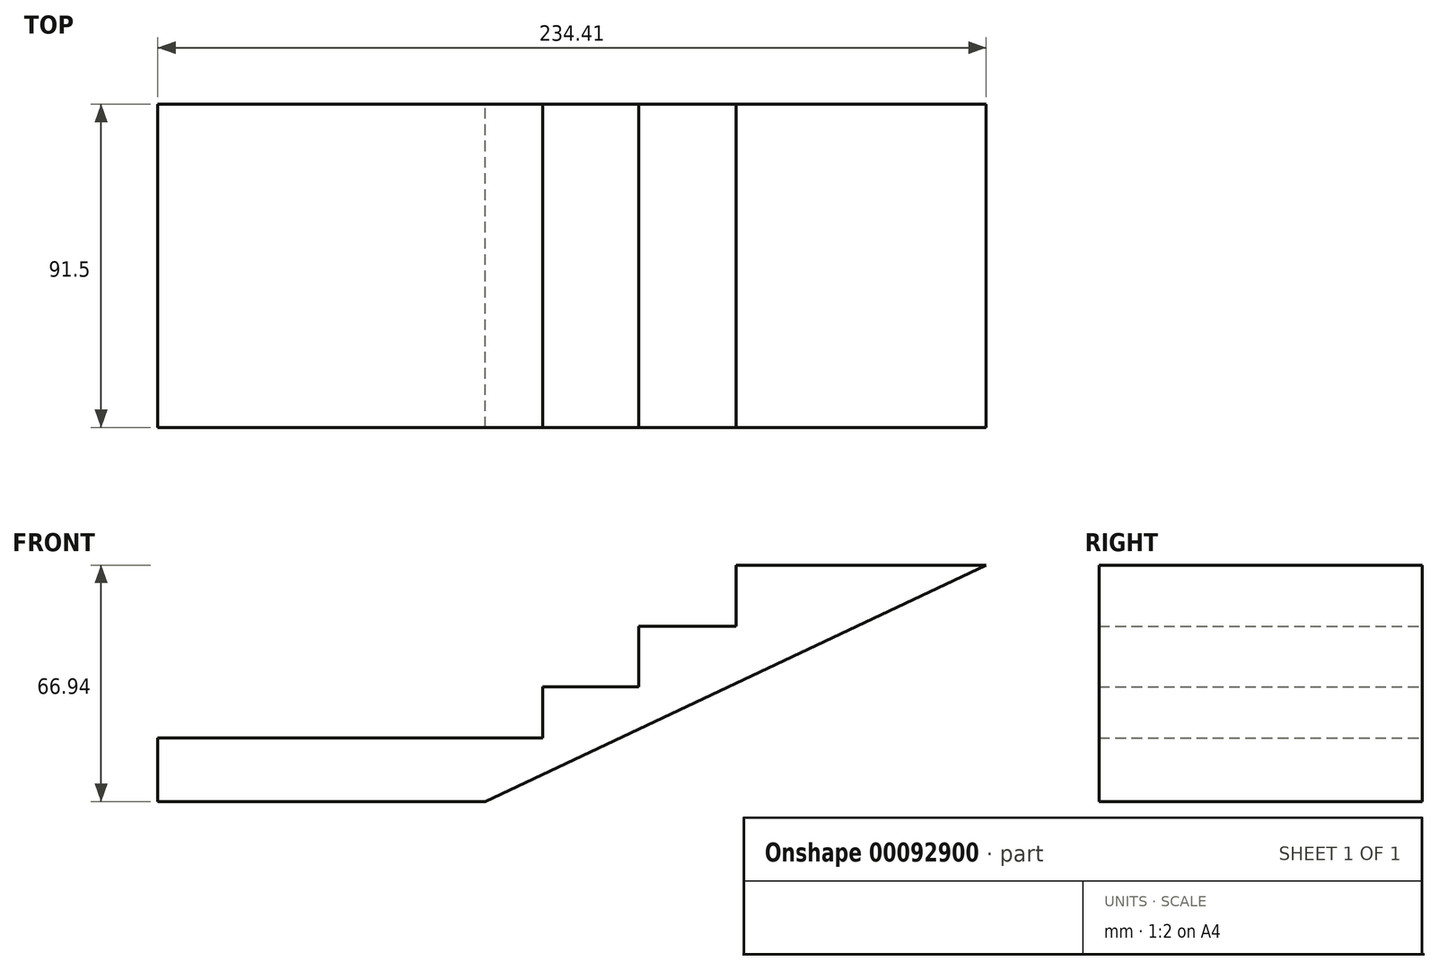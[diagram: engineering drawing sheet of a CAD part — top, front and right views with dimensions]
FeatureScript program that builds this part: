
annotation { "Feature Type Name" : "Feature", "Feature Type Description" : "" }
export const myFeature = defineFeature(function(context is Context, id is Id, definition is map)
    precondition{}
    {
        {
            var Q0;
            Q0=qCreatedBy(makeId("Front.planeOp"),FACE);
            var sketch = newSketch(context, id + "F0", { "sketchPlane" : qUnion([Q0])});
            skLineSegment(sketch, "E0", {"start": v(-0.4, -34.5) * mm, "end": v(26.75, -34.5) * mm});
            skLineSegment(sketch, "E1", {"start": v(26.75, -34.5) * mm, "end": v(26.75, -17.25) * mm});
            skLineSegment(sketch, "E2", {"start": v(26.75, -17.25) * mm, "end": v(54.25, -17.25) * mm});
            skLineSegment(sketch, "E3", {"start": v(54.25, -17.25) * mm, "end": v(54.25, 0) * mm});
            skLineSegment(sketch, "E4", {"start": v(54.25, 0) * mm, "end": v(145.75, 0) * mm});
            skLineSegment(sketch, "E5", {"start": v(-0.4, -34.5) * mm, "end": v(-0.4, -48.94) * mm});
            skLineSegment(sketch, "E6", {"start": v(-0.4, -48.94) * mm, "end": v(-109.4, -48.94) * mm});
            skLineSegment(sketch, "E7", {"start": v(-16.75, -48.94) * mm, "end": v(-16.75, -66.94) * mm});
            skLineSegment(sketch, "E8", {"start": v(-16.75, -66.94) * mm, "end": v(-109.4, -66.94) * mm});
            skLineSegment(sketch, "E9", {"start": v(-109.4, -66.94) * mm, "end": v(-109.4, -48.94) * mm});
            skLineSegment(sketch, "E10", {"start": v(-16.75, -66.94) * mm, "end": v(125, 0) * mm});
            skSolve(sketch);
        }
        {
            var Q0;
            Q0=makeQuery(id+"F0.imprint","IMPRINT",FACE,{"disambiguationData":[TD([[makeQuery(id+"F0.imprint","IMPRINT",EDGE,{"derivedFrom":sQuery(id+"F0.wireOp",EDGE,"E0")}),-1.0]])]});
            extrude(context, id + "F1", {"entities" : qUnion([Q0]), "endBound" : BoundingType.SYMMETRIC, "depth" : 91.5 * mm});
        }
        {
            var Q0;
            Q0 = qSketchRegion(id + "F0", true);
            extrude(context, id + "F2", {"entities" : qUnion([Q0]), "operationType" : NewBodyOperationType.ADD, "endBound" : BoundingType.SYMMETRIC, "depth" : 91.5 * mm});
        }
    });
